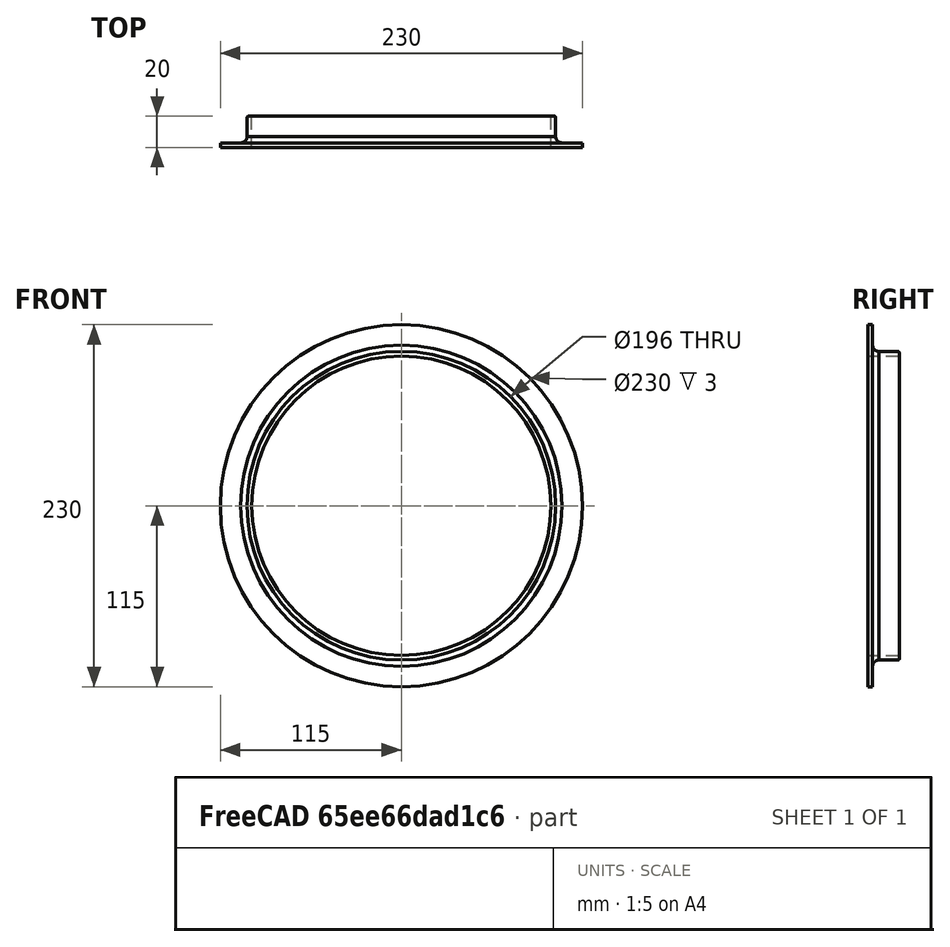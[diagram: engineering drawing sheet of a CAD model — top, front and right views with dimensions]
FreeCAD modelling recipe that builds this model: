
FCSTD DOCUMENT  (FreeCAD 0.18R16110 (Git))
Label: 7.5inducking
License: All rights reserved
LicenseURL: http://en.wikipedia.org/wiki/All_rights_reserved
objects: Sketcher::SketchObject×1, Part::Revolution×1, Part::Fillet×1
note: 3 computed .brp shape members not serialized (recipe doc carries the construction recipe); baked Part::Feature solids carry a one-line shape summary decoded from their .brp

FEATURE [Sketcher::SketchObject] Sketch
  sketch-geometry (7):
    g0: LineSegment StartX=95 StartY=0 StartZ=0 EndX=95 EndY=20 EndZ=0
    g1: LineSegment StartX=95 StartY=20 StartZ=0 EndX=98 EndY=20 EndZ=0
    g2: LineSegment StartX=95 StartY=0 StartZ=0 EndX=115 EndY=0 EndZ=0
    g3: LineSegment StartX=115 StartY=0 StartZ=0 EndX=115 EndY=3 EndZ=0
    g4: LineSegment StartX=115 StartY=3 StartZ=0 EndX=102 EndY=3 EndZ=0
    g5: LineSegment StartX=98 StartY=20 StartZ=0 EndX=98 EndY=7 EndZ=0
    g6: ArcOfCircle CenterX=102.089 CenterY=7.08903 CenterZ=0 NormalX=0 NormalY=0 NormalZ=1 AngleXU=0 Radius=4.09 StartAngle=3.16336 EndAngle=4.69062
  constraints (22):
    c: PointOnObject(g0,g-1)
    c: Vertical(g0)
    c: DistanceX(g0) = 95
    c: DistanceY(g0) = 20
    c: Coincident(g1,g0)
    c: Horizontal(g1)
    c: DistanceX(g1,g1) = 3
    c: Coincident(g0,g2)
    c: PointOnObject(g2,g-1)
    c: Coincident(g2,g3)
    c: Vertical(g3)
    c: Coincident(g3,g4)
    c: Coincident(g5,g1)
    c: Vertical(g5)
    c: Coincident(g6,g5)
    c: Coincident(g6,g4)
    c: Horizontal(g4)
    c: DistanceY(g3,g3) = 3
    c: DistanceX(g4,g4) = 13
    c: DistanceY(g5,g5) = 13
    c: Radius(g6) = 4.09
    c: DistanceX(g2,g2) = 20
FEATURE [Part::Revolution] Revolve
  Angle = 360
  Axis = (0,1,0)
  Base = (0,0,0)
  FaceMakerClass = Part::FaceMakerBullseye
  Solid = false
  Source = -> Sketch
  Symmetric = false
FEATURE [Part::Fillet] Fillet
  Base = -> Revolve
  Edges = 1 edges r=1: [Edge4]
